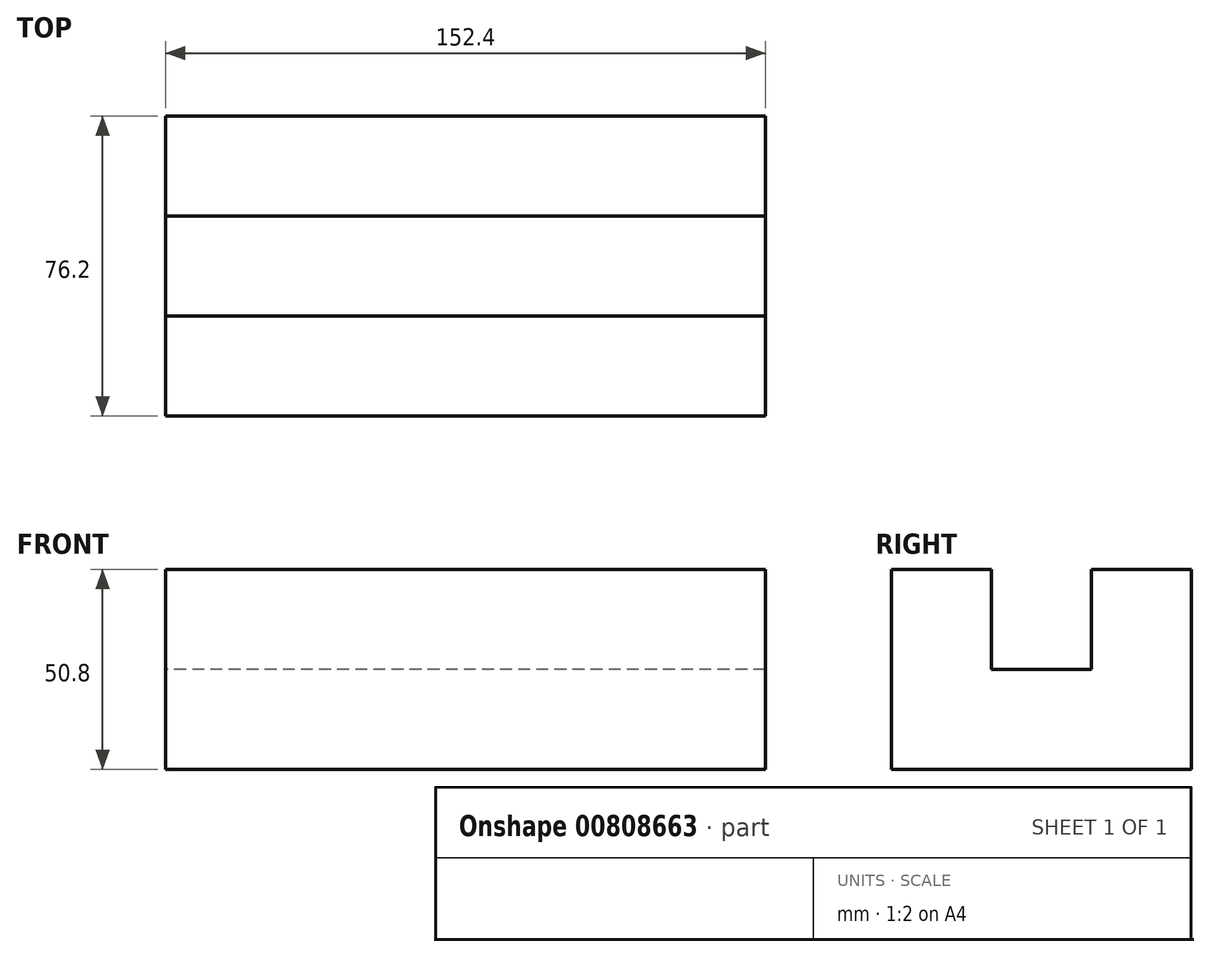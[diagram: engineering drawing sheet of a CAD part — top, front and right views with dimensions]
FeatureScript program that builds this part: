
annotation { "Feature Type Name" : "Feature", "Feature Type Description" : "" }
export const myFeature = defineFeature(function(context is Context, id is Id, definition is map)
    precondition{}
    {
        {
            var Q0;
            Q0=qCreatedBy(makeId("Right.planeOp"),FACE);
            var sketch = newSketch(context, id + "F0", { "sketchPlane" : qUnion([Q0])});
            skLineSegment(sketch, "E0", {"start": v(0, 0) * mm, "end": v(76.2, 0) * mm});
            skLineSegment(sketch, "E1", {"start": v(0, 0) * mm, "end": v(0, 50.8) * mm});
            skLineSegment(sketch, "E2", {"start": v(76.2, 0) * mm, "end": v(76.2, 50.8) * mm});
            skLineSegment(sketch, "E3", {"start": v(0, 50.8) * mm, "end": v(25.4, 50.8) * mm});
            skLineSegment(sketch, "E4", {"start": v(25.4, 50.8) * mm, "end": v(25.4, 25.4) * mm});
            skLineSegment(sketch, "E5", {"start": v(25.4, 25.4) * mm, "end": v(50.8, 25.4) * mm});
            skLineSegment(sketch, "E6", {"start": v(50.8, 25.4) * mm, "end": v(50.8, 50.8) * mm});
            skLineSegment(sketch, "E7", {"start": v(50.8, 50.8) * mm, "end": v(76.2, 50.8) * mm});
            skSolve(sketch);
        }
        {
            var Q0;
            Q0=makeQuery(id+"F0.imprint","IMPRINT",FACE,{"disambiguationData":[TD([[makeQuery(id+"F0.imprint","IMPRINT",EDGE,{"derivedFrom":sQuery(id+"F0.wireOp",EDGE,"E0")}),1.0]])]});
            extrude(context, id + "F1", {"entities" : qUnion([Q0]), "depth" : 152.4 * mm, "offsetDistance" : 25.4 * mm});
        }
    });
